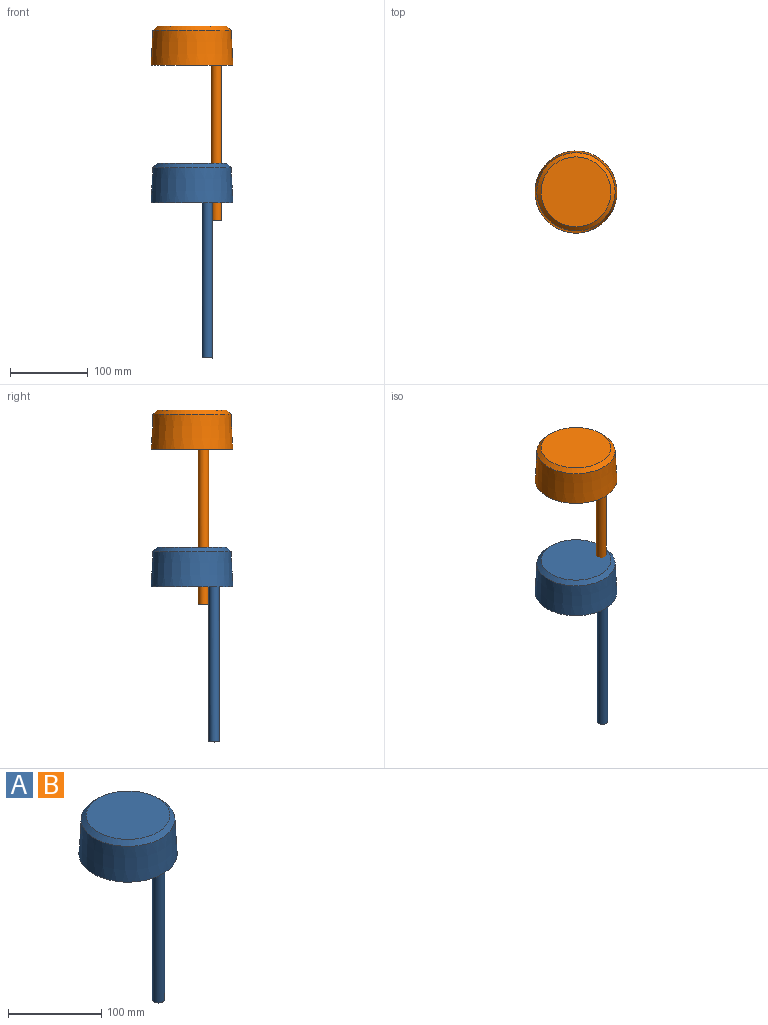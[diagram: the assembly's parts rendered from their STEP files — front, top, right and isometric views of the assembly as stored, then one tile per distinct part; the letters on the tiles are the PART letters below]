
ASSEMBLY  parts=2 mates=1
PART A: 15 faces, bbox 105.6x105.6x250.8 mm
  f0: cone r=50.12mm half-angle=3deg, axis (0,0,-1), area 14751.1mm2, adj f6,f8
  f1: plane 90.09x90.09mm, normal (0,0,1), area 6374.4mm2, adj f8
  f2: plane 27.06x25.4mm, normal (0,-1,0), area 687.3mm2, adj f6,f7,f9,f12
  f3: plane 31.83x25.4mm, normal (-1,0,0), area 808.5mm2, adj f6,f7,f9,f10
  f4: plane 27.06x25.4mm, normal (0,1,0), area 687.3mm2, adj f6,f7,f10,f11
  f5: plane 31.83x25.4mm, normal (1,0,0), area 808.5mm2, adj f6,f7,f11,f12
  f6: plane 105.57x105.57mm, normal (0,0,-1), area 7087.6mm2, adj f0,f2,f3,f4,f5,f9,f10,f11
  f7: plane 41.83x37.06mm, normal (0,0,-1), area 1528.6mm2, adj f2,f3,f4,f5,f9,f10,f11,f12
  f8: cone r=45.04mm half-angle=45deg, axis (0,0,-1), area 2273.5mm2, adj f0,f1
  f9: cylinder r=5mm len=25.4mm, axis (0,0,1), area 199.5mm2, adj f2,f3,f6,f7
  f10: cylinder r=5mm len=25.4mm, axis (0,0,-1), area 199.5mm2, adj f3,f4,f6,f7
  f11: cylinder r=5mm len=25.4mm, axis (0,0,1), area 199.5mm2, adj f4,f5,f6,f7
  f12: cylinder r=5mm len=25.4mm, axis (0,0,-1), area 199.5mm2, adj f2,f5,f6,f7
  f13: cylinder r=6.62mm len=200mm, axis (0,0,1), area 8322.6mm2, adj f6,f14
  f14: plane 13.25x13.25mm, normal (0,0,-1), area 137.8mm2, adj f13
PART B: same geometry as A
PLACE A rot(axis=(0,0,-1),30deg) t=(-80.12,40.42,-187.28)mm
PLACE B rot(axis=(0.01,1,0),0deg) t=(-80.12,40.42,-10)mm
MATE cylindrical A.f0 <-> B.f0  axis (0,0,-1) through (-80.12,40.42,-212.68)mm
